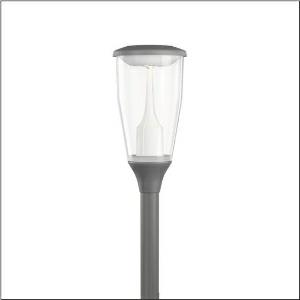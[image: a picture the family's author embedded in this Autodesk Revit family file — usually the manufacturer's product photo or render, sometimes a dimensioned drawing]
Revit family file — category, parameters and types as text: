
# Revit family: dl_11_iq___p1_0a_5xa5565bf14hp00022_ddba
name_source: partatom
category: Lighting Fixtures
units: mm (PartAtom-declared; Revit-internal decimal feet)

## family parameters
Cut with Voids When Loaded = No
Host = Face
Light Source = No
Part Type = Normal
Room Calculation Point = No
Round Connector Dimension = Use Diameter
Shared = No

## types (1)
- --- (1 x LED, 3950 lm, 33.6 W, 2200K)
    Apparent Load = 34 VA
    CIE Flux Codes = 33 63 91 94 100
    Color Rendering = 70
    Color Temperature = 2200K
    Default Elevation = 1800 mm
    Description = DL 11 iQ, mast luminaire, Module 540 iQ-SR, primary light control with 3 zone facetted reflector, of plastic, silver coated, highly specular, structured, primary optical cover: cover, of PMMA, transparent, light distribution: P1.0a, light emission: direct distribution, primary light characteristic: asymmetric, installation type: post-top, LED, High Power LED, light colour: 722, colour temperature: 2200K, control gear: iQ Street-Remote, control: Street-Remote, Auto-Match, Temp-Guard, Lumen-Switch, Night-Set, Smart-Wire, Light-Fading, Desk-Remote (wireless, voltage-free reading and setting of iQ features in the workshop via application-optimized NFC function/RFID function), optimised constant luminous flux control (CLO 2.0), mains connection: 220..240V, AC, 50/60Hz, connection cable pre-assembled, cable length: 5,5m, start of lifetime: 34W, end of service life: 36W, luminaire housing, upper part, of diecast aluminium, coated, SITECO metallic grey (DB 702S), spigot size: 60mm (post-top), mounting height: 3..5m, post-top mast mounting element, of diecast aluminium, coated, SITECO metallic grey (DB 702S), Module 540 iQ-SR, traffic white (RAL 9016), equipment: Power, protection rating (complete): IP66, insulation class (complete): insulation class II (safety insulation), certification: CE, ENEC, ENEC+, VDE, impact resistance: IK07, packaging unit: 1 piece

Light Distribution: P1.0a
    Height = 665 mm
    Lamp = 1 x LED
    Lamp Light Flux = 3950 lm
    Lamp Power = 33.6 W
    Lamp count = 1
    Length = 334 mm
    Luminous efficacy = 118 lm/W
    Manufacturer = Siteco
    ModVariant = No
    Model = 5XA5565BF14HP00022
    Number of Poles = 1
    OnlyDefault = Yes
    Power Factor = 1
    Product Name = DL 11 iQ | P1.0a
    Product group = mast luminaire | pylon top
    ProductGroupID = 6100
    Protection Class = Protection class II
    Protection Degree = IP 66
    RLX_Detail_Level = 1
    RLX_Emergency_Light_Flux = 0 lm
    RLX_Emergency_Type = 0
    RLX_Emergency_Type_DB = No
    RlxData = <blob elided: 105229 chars, md5=59c20f04>
    Socket = socket
    Standby Power = 0 W
    System Light Flux = 3950 lm
    System Power = 34 W
    Type Comments = factory setting: luminous flux: 100 % | dim-lin: 254 | 695 mA
    Type Image = l_1258354.jpg
    URL = http://relux.com
    VarID = @adj_040045
    Voltage = 0 V
    Weight = 0.00 kg
    Width = 0 mm  [stored 0 ft]

note: [stored X ft] marks values corroborated as IEEE doubles in the binary element streams (Revit-internal decimal feet)

## geometry (parser evidence)
native form markers: Blend x4, Sweep x12
no freeform markers — native parametric forms only
